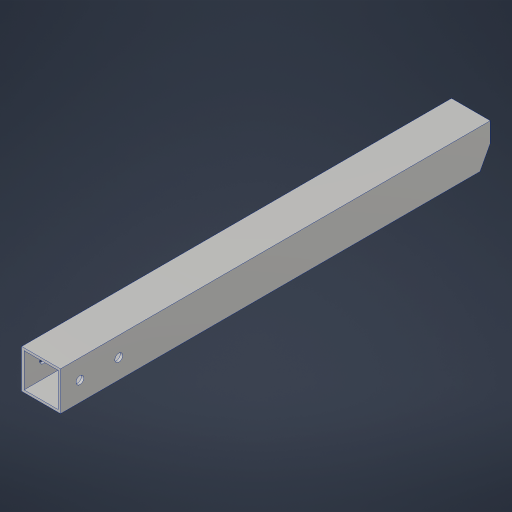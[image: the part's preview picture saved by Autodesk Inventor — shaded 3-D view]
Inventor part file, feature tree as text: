
AUTODESK INVENTOR PART (.ipt)
format: ipt  version: 2023.4 (Build 274418000, 418)  size: 200,192 bytes
history: native  units: in
note: dims shown in document units (in); Inventor stores cm internally (conversion verified against a paired STEP export)
features: extrude x2, sketch x2, projected_geometry x2, hole x1
ambient origin geometry x8: Origin, YZ Plane, XZ Plane, XY Plane, X Axis, Y Axis, Z Axis, Center Point
bodies: Solid1 (feature_tree)
feature tree (7):
  extrude  "Extrusion1"  Depth=1.0in
  hole  "Hole1"  [1 undecoded]
  extrude  "Extrusion2"  Depth=1.0in TaperAngle=0.0deg
  sketch  "Sketch2"  dims[d4=0.0in d5=1.0in]
  sketch  "Sketch3"  dims[d6=0.5in d7=0.201in d8=0.75in d9=0.385in d10=0.25in d11=0.5635in d12=1.0in d13=0.8108in d14=0.1924in d15=1.0in d16=0.0in]
  projected_geometry  "Projected Loop1"
  projected_geometry  "Project Cut Edges1"
note: 1 required parameter value undecoded (feature->parameter linkage not recoverable at this tier; creation-order binding heuristic only, values carry confidence <= 0.55)
